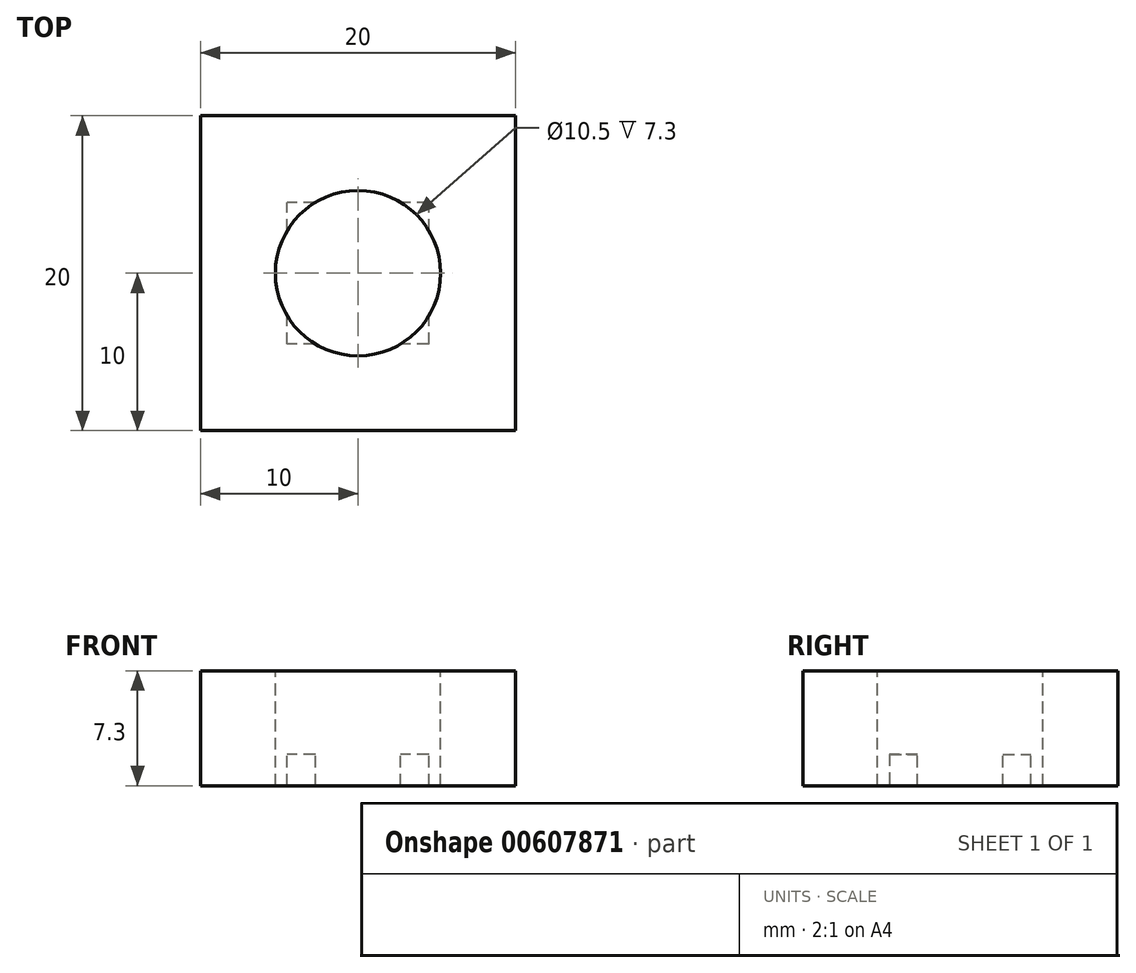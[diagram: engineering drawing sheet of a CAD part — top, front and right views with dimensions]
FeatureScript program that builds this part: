
annotation { "Feature Type Name" : "Feature", "Feature Type Description" : "" }
export const myFeature = defineFeature(function(context is Context, id is Id, definition is map)
    precondition{}
    {
        {
            var Q0;
            Q0=qCreatedBy(makeId("Top.planeOp"),FACE);
            var sketch = newSketch(context, id + "F0", { "sketchPlane" : qUnion([Q0])});
            skLineSegment(sketch, "E0.bottom", {"start": v(10, -10) * mm, "end": v(-10, -10) * mm});
            skLineSegment(sketch, "E0.top", {"start": v(10, 10) * mm, "end": v(-10, 10) * mm});
            skLineSegment(sketch, "E0.left", {"start": v(10, -10) * mm, "end": v(10, 10) * mm});
            skLineSegment(sketch, "E0.right", {"start": v(-10, -10) * mm, "end": v(-10, 10) * mm});
            skPoint(sketch, "E0.middle", {"position": v(0, 0) * mm});
            skLineSegment(sketch, "E1.bottom", {"start": v(4.5, -4.5) * mm, "end": v(-4.5, -4.5) * mm});
            skLineSegment(sketch, "E1.top", {"start": v(4.5, 4.5) * mm, "end": v(-4.5, 4.5) * mm});
            skLineSegment(sketch, "E1.left", {"start": v(4.5, -4.5) * mm, "end": v(4.5, 4.5) * mm});
            skLineSegment(sketch, "E1.right", {"start": v(-4.5, -4.5) * mm, "end": v(-4.5, 4.5) * mm});
            skSolve(sketch);
        }
        {
            var Q0;
            Q0=makeQuery(id+"F0.imprint","IMPRINT",FACE,{"disambiguationData":[TD([[makeQuery(id+"F0.imprint","IMPRINT",EDGE,{"derivedFrom":sQuery(id+"F0.wireOp",EDGE,"E0.bottom")}),-1.0]])]});
            extrude(context, id + "F1", {"entities" : qUnion([Q0]), "depth" : 2 * mm, "offsetDistance" : 25 * mm});
        }
        {
            var Q0;
            Q0=makeQuery(id+"F1.opExtrude","CAP_FACE",FACE,{"disambiguationData":[OSD([sQuery(id+"F0.wireOp",EDGE,"E0.bottom"),sQuery(id+"F0.wireOp",EDGE,"E0.top"),sQuery(id+"F0.wireOp",EDGE,"E0.left"),sQuery(id+"F0.wireOp",EDGE,"E0.right"),sQuery(id+"F0.wireOp",EDGE,"E1.bottom"),sQuery(id+"F0.wireOp",EDGE,"E1.top"),sQuery(id+"F0.wireOp",EDGE,"E1.left"),sQuery(id+"F0.wireOp",EDGE,"E1.right")])],"isStart":false});
            var sketch = newSketch(context, id + "F2", { "sketchPlane" : qUnion([Q0])});
            skLineSegment(sketch, "E2.bottom", {"start": v(-10, 10) * mm, "end": v(10, 10) * mm});
            skLineSegment(sketch, "E2.top", {"start": v(-10, -10) * mm, "end": v(10, -10) * mm});
            skLineSegment(sketch, "E2.left", {"start": v(-10, 10) * mm, "end": v(-10, -10) * mm});
            skLineSegment(sketch, "E2.right", {"start": v(10, 10) * mm, "end": v(10, -10) * mm});
            skPoint(sketch, "E2.middle", {"position": v(0, 0) * mm});
            skSolve(sketch);
        }
        {
            var Q0;
            Q0 = qSketchRegion(id + "F2", true);
            extrude(context, id + "F3", {"entities" : qUnion([Q0]), "operationType" : NewBodyOperationType.ADD, "depth" : 5.3 * mm, "offsetDistance" : 25 * mm});
        }
        {
            var Q0;
            Q0=makeQuery(id+"F3.opExtrude","CAP_FACE",FACE,{"disambiguationData":[OSD([sQuery(id+"F2.wireOp",EDGE,"E2.bottom"),sQuery(id+"F2.wireOp",EDGE,"E2.top"),sQuery(id+"F2.wireOp",EDGE,"E2.left"),sQuery(id+"F2.wireOp",EDGE,"E2.right")])],"isStart":false});
            var sketch = newSketch(context, id + "F4", { "sketchPlane" : qUnion([Q0])});
            skCircle(sketch, "E3", {"center": v(0, 0) * mm, "radius": 5.25 * mm});
            skSolve(sketch);
        }
        {
            var Q0;
            Q0=makeQuery(id+"F4.imprint","IMPRINT",FACE,{"disambiguationData":[TD([[makeQuery(id+"F4.imprint","IMPRINT",EDGE,{"derivedFrom":sQuery(id+"F4.wireOp",EDGE,"E3")}),1.0]])]});
            extrude(context, id + "F5", {"entities" : qUnion([Q0]), "operationType" : NewBodyOperationType.REMOVE, "oppositeDirection" : true, "depth" : 10 * mm, "offsetDistance" : 25 * mm});
        }
    });
